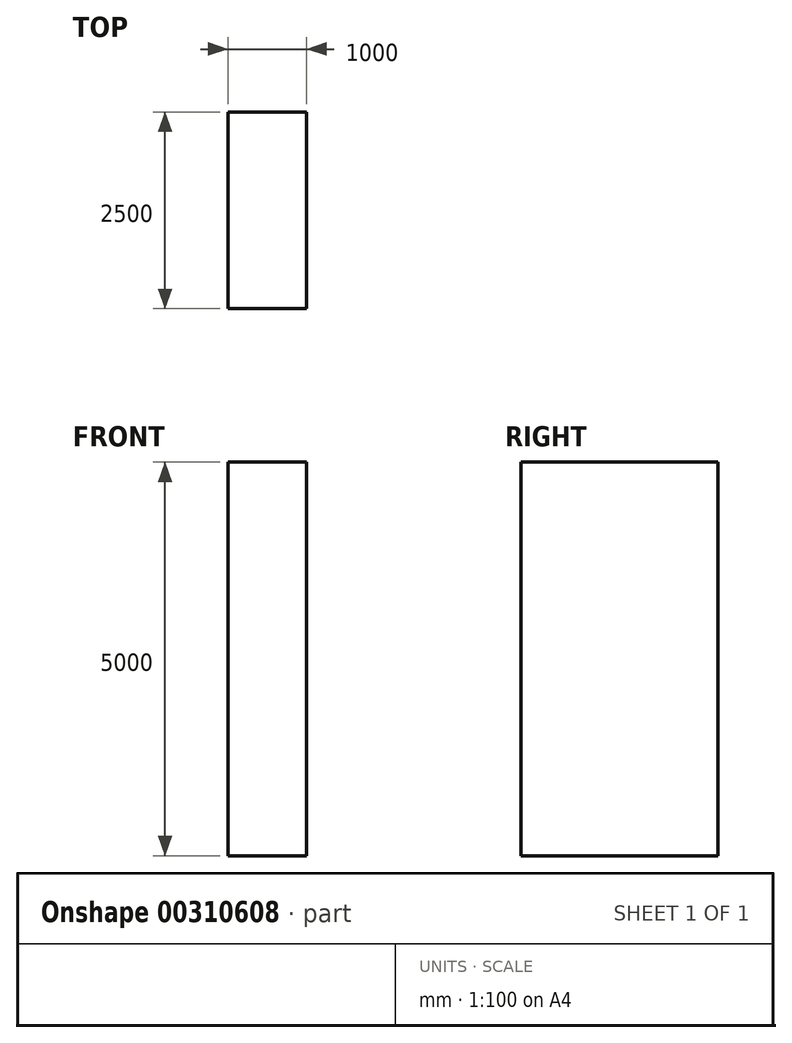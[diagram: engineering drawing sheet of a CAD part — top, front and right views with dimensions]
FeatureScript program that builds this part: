
annotation { "Feature Type Name" : "Feature", "Feature Type Description" : "" }
export const myFeature = defineFeature(function(context is Context, id is Id, definition is map)
    precondition{}
    {
        {
            var Q0;
            Q0=qCreatedBy(makeId("Right.planeOp"),FACE);
            var sketch = newSketch(context, id + "F0", { "sketchPlane" : qUnion([Q0])});
            skLineSegment(sketch, "E0.bottom", {"start": v(-1250, -2500) * mm, "end": v(1250, -2500) * mm});
            skLineSegment(sketch, "E0.top", {"start": v(-1250, 2500) * mm, "end": v(1250, 2500) * mm});
            skLineSegment(sketch, "E0.left", {"start": v(-1250, -2500) * mm, "end": v(-1250, 2500) * mm});
            skLineSegment(sketch, "E0.right", {"start": v(1250, -2500) * mm, "end": v(1250, 2500) * mm});
            skPoint(sketch, "E0.middle", {"position": v(0, 0) * mm});
            skSolve(sketch);
        }
        {
            var Q0;
            Q0 = qSketchRegion(id + "F0", true);
            extrude(context, id + "F1", {"entities" : qUnion([Q0]), "depth" : 1000 * mm});
        }
    });
